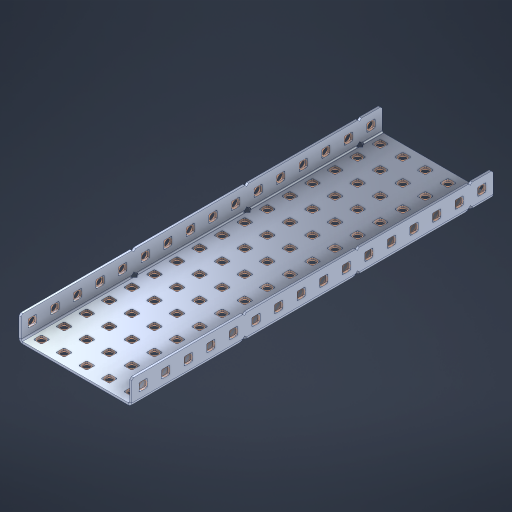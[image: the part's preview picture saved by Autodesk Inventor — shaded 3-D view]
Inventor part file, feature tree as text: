
AUTODESK INVENTOR PART (.ipt)
format: ipt  version: 2023 (Build 270158000, 158)  size: 1,438,720 bytes
history: native  units: in
note: dims shown in document units (in); Inventor stores cm internally (conversion verified against a paired STEP export)
features: other x117, extrude x111, sheet_metal_op x10, sketch x8, mirror x1, pattern_linear x1, chamfer x1
ambient origin geometry x8: Origin, YZ Plane, XZ Plane, XY Plane, X Axis, Y Axis, Z Axis, Center Point
bodies: Solid1 (feature_tree), Body (feature_tree)
feature tree (249):
  other  "Flange Pattern Plane"
  sheet_metal_op  "Flange Pattern"
  sheet_metal_op  "Body Pattern"
  other  "Arc Length"
  mirror  "Notch Mirror"
  pattern_linear  "Notch Pattern"  Spacing1=0.1875in  [1 undecoded]
  chamfer  "End Chamfer"
  extrude  "Half Cut"  Depth=0.0469in
  sketch  "Sketch1"  dims[d0=2.5in]
  other  "Plate1"
  sketch  "Sketch2"  dims[d1=8.0in]
  other  "Plate2"
  sheet_metal_op  "Bend1"
  sheet_metal_op  "Corner1"
  sketch  "Sketch3"  dims[d2=0.0469in]
  other  "Flange Pattern Sketch"
  sketch  "Sketch7"  dims[d3=0.0469in]
  other  "Srf1"
  other  "Srf2"
  sketch  "Sketch8"  dims[d4=0.0234in]
  sketch  "Sketch9"  dims[d5=0.0938in]
  other  "Srf91"
  sheet_metal_op  "Body Pattern Sketch"
  other  "Srf92"
  sketch  "Sketch13"  dims[d6=0.0469in]
  sketch  "Sketch14"  dims[d7=0.5in d8=90.0deg d9=0.0312in d10=0.1875in d11=0.0469in d12=0.0469in d16=0.182in d17=0.02in d18=0.0469in d19=0.0in d20=0.25in d21=0.25in d46=0.172in d47=1.0in d48=0.0in d49=0.182in d50=0.02in d51=0.25in d52=0.25in d53=0.0469in d54=0.0in d55=0.172in d56=1.0in d57=0.0in d60=6.2992in d62=0.5in d63=1.9685in d65=0.5in d85=0.1227in d86=0.1659in d88=0.04in d89=0.0469in d90=0.0in d91=0.04in d92=0.0491in d95=2.5in d96=0.04in d97=0.25in d98=45.0deg d101=0.0in d102=2.497in d131=2.5in d132=6.2992in d134=0.5in d139=0.5in]
  other  "Srf856"
  other  "Srf1310"
  other  "Srf1311"
  other  "Srf1312"
  other  "Srf1376"
  other  "Srf1377"
  other  "Srf1728"
  other  "Srf1755"
  other  "Srf1878"
  other  "Srf1879"
  other  "Srf1880"
  other  "Srf1881"
  other  "Srf1882"
  other  "Srf1883"
  other  "Srf1884"
  other  "Srf1885"
  other  "Srf1886"
  other  "Srf1887"
  other  "Srf1888"
  other  "Srf1889"
  other  "Srf1890"
  other  "Srf1891"
  other  "Srf1892"
  other  "Srf1893"
  other  "Srf1894"
  other  "Srf1895"
  other  "Srf1896"
  other  "Srf1897"
  other  "Srf1898"
  other  "Srf1899"
  other  "Srf1900"
  other  "Srf1901"
  other  "Srf1902"
  other  "Srf1903"
  other  "Srf1942"
  other  "Srf1943"
  other  "Srf1944"
  other  "Srf1945"
  other  "Srf1946"
  other  "Srf1947"
  other  "Srf1948"
  other  "Srf1949"
  other  "Srf1950"
  other  "Srf1951"
  other  "Srf1952"
  other  "Srf1953"
  other  "Srf1954"
  other  "Srf1955"
  other  "Srf1956"
  other  "Srf1957"
  other  "Srf1958"
  other  "Srf1959"
  other  "Srf1960"
  other  "Srf1961"
  other  "Srf1962"
  other  "Srf1963"
  other  "Srf1964"
  other  "Srf1965"
  other  "Srf1966"
  other  "Srf1967"
  other  "Srf1968"
  other  "Srf1969"
  other  "Srf1970"
  other  "Srf2146"
  other  "Srf2147"
  other  "Srf2148"
  other  "Srf2149"
  other  "Srf2150"
  other  "Srf2151"
  other  "Srf2152"
  other  "Srf2153"
  other  "Srf2154"
  other  "Srf2155"
  other  "Srf2156"
  other  "Srf2157"
  other  "Srf2158"
  other  "Srf2159"
  other  "Srf2160"
  other  "Srf2161"
  other  "Srf2162"
  other  "Srf2163"
  other  "Srf2164"
  other  "Srf2165"
  other  "Srf2166"
  other  "Srf2167"
  other  "Srf2168"
  other  "Srf2169"
  other  "Srf2170"
  other  "Srf2171"
  other  "Srf2172"
  other  "Srf2173"
  other  "Srf2174"
  other  "Srf2175"
  other  "Srf2176"
  other  "Srf2177"
  other  "Srf2178"
  other  "Srf2179"
  other  "Srf2180"
  other  "Srf2181"
  other  "Srf2182"
  other  "Srf2183"
  other  "Srf2184"
  other  "Srf2185"
  other  "Srf2186"
  other  "Srf2187"
  other  "Srf2188"
  other  "Srf2189"
  other  "Srf2190"
  sheet_metal_op  "Flange Stamp"
  sheet_metal_op  "Flange Circle"
  sheet_metal_op  "Body Stamp"
  sheet_metal_op  "Body Circle"
  sheet_metal_op  "Notch"
  extrude  "ExtrusionSrf2"  Depth=0.0469in
  extrude  "ExtrusionSrf92"  Depth=2.5in
  extrude  "ExtrusionSrf856"  Depth=0.02in
  extrude  "ExtrusionSrf1310"  Depth=0.0469in
  extrude  "ExtrusionSrf1311"  TaperAngle=0.0deg  [1 undecoded]
  extrude  "ExtrusionSrf1312"  Depth=0.25in
  extrude  "ExtrusionSrf1376"  Depth=0.25in
  extrude  "ExtrusionSrf1377"  Depth=2.5in
  extrude  "ExtrusionSrf1728"  Depth=2.5in TaperAngle=0.0deg
  extrude  "ExtrusionSrf1755"  Depth=2.5in
  extrude  "ExtrusionSrf1878"  Depth=0.02in
  extrude  "ExtrusionSrf1879"  Depth=0.25in
  extrude  "ExtrusionSrf1880"  Depth=0.25in
  extrude  "ExtrusionSrf1881"  Depth=0.0469in
  extrude  "ExtrusionSrf1882"  TaperAngle=0.0deg  [1 undecoded]
  extrude  "ExtrusionSrf1883"  Depth=2.5in
  extrude  "ExtrusionSrf1884"  Depth=2.5in TaperAngle=0.0deg
  extrude  "ExtrusionSrf1885"  Depth=2.5in
  extrude  "ExtrusionSrf1886"  Depth=2.5in
  extrude  "ExtrusionSrf1887"  Depth=2.5in
  extrude  "ExtrusionSrf1888"  Depth=2.5in
  extrude  "ExtrusionSrf1889"  Depth=2.5in
  extrude  "ExtrusionSrf1890"  Depth=0.0469in
  extrude  "ExtrusionSrf1891"  TaperAngle=0.0deg  [1 undecoded]
  extrude  "ExtrusionSrf1892"  Depth=2.5in
  extrude  "ExtrusionSrf1893"  Depth=2.5in
  extrude  "ExtrusionSrf1894"  Depth=2.5in
  extrude  "ExtrusionSrf1895"  Depth=0.25in TaperAngle=45.0deg
  extrude  "ExtrusionSrf1896"  TaperAngle=0.0deg  [1 undecoded]
  extrude  "ExtrusionSrf1897"  Depth=2.5in
  extrude  "ExtrusionSrf1898"  Depth=2.5in
  extrude  "ExtrusionSrf1899"  Depth=2.5in
  extrude  "ExtrusionSrf1900"  Depth=2.5in
  extrude  "ExtrusionSrf1901"  Depth=2.5in
  extrude  "ExtrusionSrf1902"  [1 undecoded]
  extrude  "ExtrusionSrf1903"  [1 undecoded]
  extrude  "ExtrusionSrf1942"  [1 undecoded]
  extrude  "ExtrusionSrf1943"  [1 undecoded]
  extrude  "ExtrusionSrf1944"  [1 undecoded]
  extrude  "ExtrusionSrf1945"  [1 undecoded]
  extrude  "ExtrusionSrf1946"  [1 undecoded]
  extrude  "ExtrusionSrf1947"  [1 undecoded]
  extrude  "ExtrusionSrf1948"  [1 undecoded]
  extrude  "ExtrusionSrf1949"  [1 undecoded]
  extrude  "ExtrusionSrf1950"  [1 undecoded]
  extrude  "ExtrusionSrf1951"  [1 undecoded]
  extrude  "ExtrusionSrf1952"  [1 undecoded]
  extrude  "ExtrusionSrf1953"  [1 undecoded]
  extrude  "ExtrusionSrf1954"  [1 undecoded]
  extrude  "ExtrusionSrf1955"  [1 undecoded]
  extrude  "ExtrusionSrf1956"  [1 undecoded]
  extrude  "ExtrusionSrf1957"  [1 undecoded]
  extrude  "ExtrusionSrf1958"  [1 undecoded]
  extrude  "ExtrusionSrf1959"  [1 undecoded]
  extrude  "ExtrusionSrf1960"  [1 undecoded]
  extrude  "ExtrusionSrf1961"  [1 undecoded]
  extrude  "ExtrusionSrf1962"  [1 undecoded]
  extrude  "ExtrusionSrf1963"  [1 undecoded]
  extrude  "ExtrusionSrf1964"  [1 undecoded]
  extrude  "ExtrusionSrf1965"  [1 undecoded]
  extrude  "ExtrusionSrf1966"  [1 undecoded]
  extrude  "ExtrusionSrf1967"  [1 undecoded]
  extrude  "ExtrusionSrf1968"  [1 undecoded]
  extrude  "ExtrusionSrf1969"  [1 undecoded]
  extrude  "ExtrusionSrf1970"  [1 undecoded]
  extrude  "ExtrusionSrf2146"  [1 undecoded]
  extrude  "ExtrusionSrf2147"  [1 undecoded]
  extrude  "ExtrusionSrf2148"  [1 undecoded]
  extrude  "ExtrusionSrf2149"  [1 undecoded]
  extrude  "ExtrusionSrf2150"  [1 undecoded]
  extrude  "ExtrusionSrf2151"  [1 undecoded]
  extrude  "ExtrusionSrf2152"  [1 undecoded]
  extrude  "ExtrusionSrf2153"  [1 undecoded]
  extrude  "ExtrusionSrf2154"  [1 undecoded]
  extrude  "ExtrusionSrf2155"  [1 undecoded]
  extrude  "ExtrusionSrf2156"  [1 undecoded]
  extrude  "ExtrusionSrf2157"  [1 undecoded]
  extrude  "ExtrusionSrf2158"  [1 undecoded]
  extrude  "ExtrusionSrf2159"  [1 undecoded]
  extrude  "ExtrusionSrf2160"  [1 undecoded]
  extrude  "ExtrusionSrf2161"  [1 undecoded]
  extrude  "ExtrusionSrf2162"  [1 undecoded]
  extrude  "ExtrusionSrf2163"  [1 undecoded]
  extrude  "ExtrusionSrf2164"  [1 undecoded]
  extrude  "ExtrusionSrf2165"  [1 undecoded]
  extrude  "ExtrusionSrf2166"  [1 undecoded]
  extrude  "ExtrusionSrf2167"  [1 undecoded]
  extrude  "ExtrusionSrf2168"  [1 undecoded]
  extrude  "ExtrusionSrf2169"  [1 undecoded]
  extrude  "ExtrusionSrf2170"  [1 undecoded]
  extrude  "ExtrusionSrf2171"  [1 undecoded]
  extrude  "ExtrusionSrf2172"  [1 undecoded]
  extrude  "ExtrusionSrf2173"  [1 undecoded]
  extrude  "ExtrusionSrf2174"  [1 undecoded]
  extrude  "ExtrusionSrf2175"  [1 undecoded]
  extrude  "ExtrusionSrf2176"  [1 undecoded]
  extrude  "ExtrusionSrf2177"  [1 undecoded]
  extrude  "ExtrusionSrf2178"  [1 undecoded]
  extrude  "ExtrusionSrf2179"  [1 undecoded]
  extrude  "ExtrusionSrf2180"  [1 undecoded]
  extrude  "ExtrusionSrf2181"  [1 undecoded]
  extrude  "ExtrusionSrf2182"  [1 undecoded]
  extrude  "ExtrusionSrf2183"  [1 undecoded]
  extrude  "ExtrusionSrf2184"  [1 undecoded]
  extrude  "ExtrusionSrf2185"  [1 undecoded]
  extrude  "ExtrusionSrf2186"  [1 undecoded]
  extrude  "ExtrusionSrf2187"  [1 undecoded]
  extrude  "ExtrusionSrf2188"  [1 undecoded]
  extrude  "ExtrusionSrf2189"  [1 undecoded]
  extrude  "ExtrusionSrf2190"  [1 undecoded]
note: 81 required parameter values undecoded (feature->parameter linkage not recoverable at this tier; creation-order binding heuristic only, values carry confidence <= 0.55)
